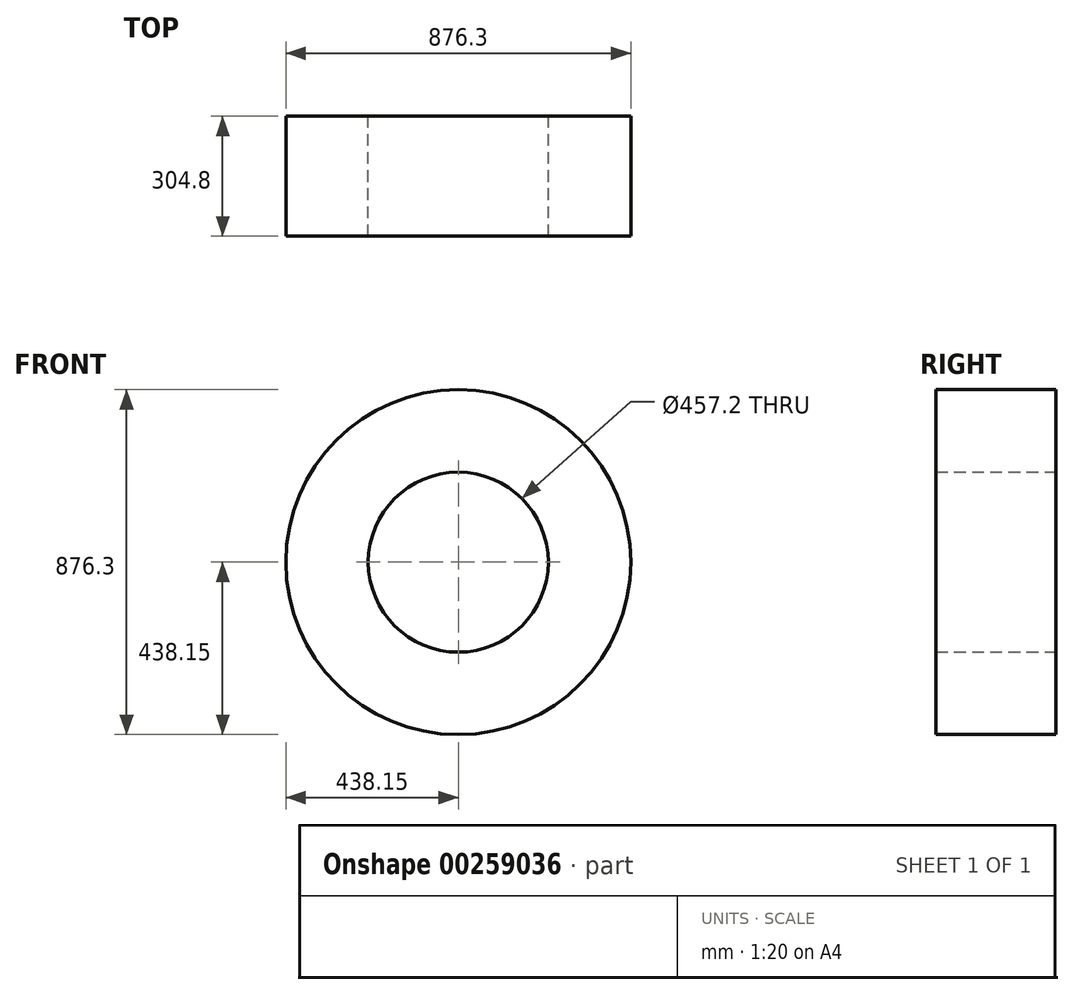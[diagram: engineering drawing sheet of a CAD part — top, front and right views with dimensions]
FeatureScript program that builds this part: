
annotation { "Feature Type Name" : "Feature", "Feature Type Description" : "" }
export const myFeature = defineFeature(function(context is Context, id is Id, definition is map)
    precondition{}
    {
        {
            var Q0;
            Q0=qCreatedBy(makeId("Front.planeOp"),FACE);
            var sketch = newSketch(context, id + "F0", { "sketchPlane" : qUnion([Q0])});
            skCircle(sketch, "E0", {"center": v(0, 0) * mm, "radius": 438.15 * mm});
            skCircle(sketch, "E1", {"center": v(0, 0) * mm, "radius": 228.6 * mm});
            skSolve(sketch);
        }
        {
            var Q0;
            Q0=makeQuery(id+"F0.imprint","IMPRINT",FACE,{"disambiguationData":[TD([[makeQuery(id+"F0.imprint","IMPRINT",EDGE,{"derivedFrom":sQuery(id+"F0.wireOp",EDGE,"E0")}),1.0]])]});
            extrude(context, id + "F1", {"entities" : qUnion([Q0]), "depth" : 76.2 * mm, "hasSecondDirection" : true, "secondDirectionOppositeDirection" : true, "secondDirectionDepth" : 228.6 * mm});
        }
    });
